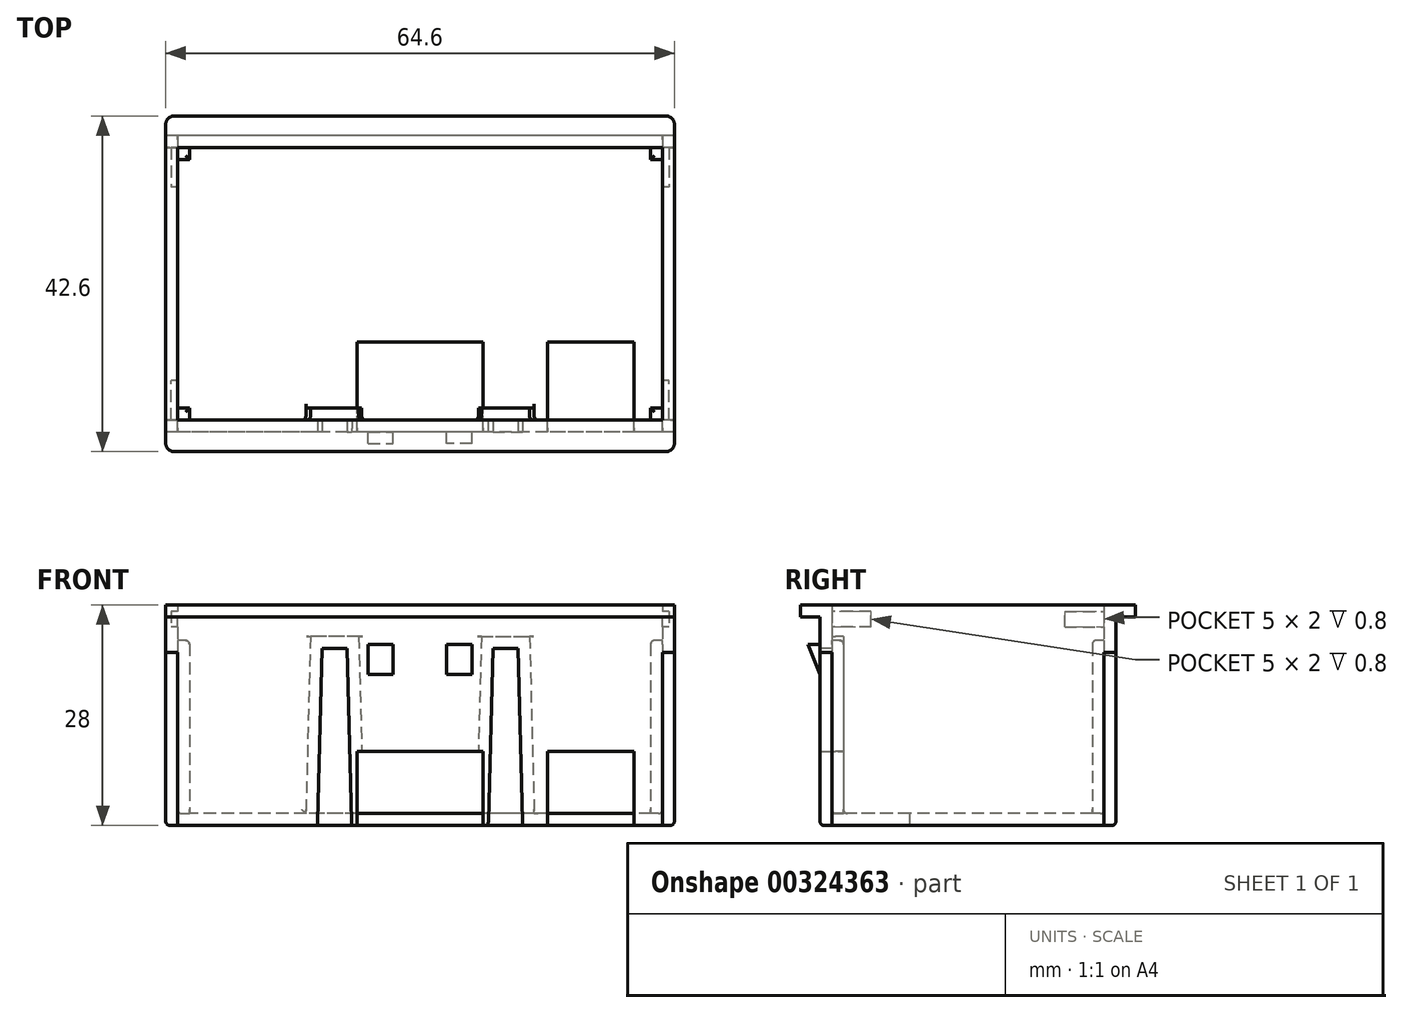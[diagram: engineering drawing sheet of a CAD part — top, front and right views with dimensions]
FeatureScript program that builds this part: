
annotation { "Feature Type Name" : "Feature", "Feature Type Description" : "" }
export const myFeature = defineFeature(function(context is Context, id is Id, definition is map)
    precondition{}
    {
        {
            var Q0;
            Q0=qCreatedBy(makeId("Top.planeOp"),FACE);
            var sketch = newSketch(context, id + "F0", { "sketchPlane" : qUnion([Q0])});
            skLineSegment(sketch, "E0.bottom", {"start": v(32.3, 18.8) * mm, "end": v(-32.3, 18.8) * mm});
            skLineSegment(sketch, "E0.top", {"start": v(32.3, -18.8) * mm, "end": v(-32.3, -18.8) * mm});
            skLineSegment(sketch, "E0.left", {"start": v(32.3, 18.8) * mm, "end": v(32.3, -18.8) * mm});
            skLineSegment(sketch, "E0.right", {"start": v(-32.3, 18.8) * mm, "end": v(-32.3, -18.8) * mm});
            skPoint(sketch, "E0.middle", {"position": v(0, 0) * mm});
            skSolve(sketch);
        }
        {
            var Q0;
            Q0=makeQuery(id+"F0.imprint","IMPRINT",FACE,{"disambiguationData":[TD([[makeQuery(id+"F0.imprint","IMPRINT",EDGE,{"derivedFrom":sQuery(id+"F0.wireOp",EDGE,"E0.bottom")}),1.0]])]});
            extrude(context, id + "F1", {"entities" : qUnion([Q0]), "depth" : 28 * mm});
        }
        {
            var Q0;
            Q0=makeQuery(id+"F1.opExtrude","SWEPT_FACE",FACE,{"disambiguationData":[OSD([sQuery(id+"F0.wireOp",EDGE,"E0.top")])]});
            var sketch = newSketch(context, id + "F2", { "sketchPlane" : qUnion([Q0])});
            skLineSegment(sketch, "E1", {"start": v(0, 0) * mm, "end": v(0, 51.62) * mm, "construction": true});
            skLineSegment(sketch, "E2.0", {"start": v(-8.66, 0) * mm, "end": v(-13.04, 0) * mm});
            skLineSegment(sketch, "E3", {"start": v(-9.25, 22.5) * mm, "end": v(-12.45, 22.5) * mm});
            skLineSegment(sketch, "E4", {"start": v(-12.45, 22.5) * mm, "end": v(-13.04, 0) * mm});
            skPoint(sketch, "E5.orphan", {"position": v(32.3, 0) * mm});
            skPoint(sketch, "E6.orphan", {"position": v(-32.3, 0) * mm});
            skLineSegment(sketch, "E7", {"start": v(-9.25, 22.5) * mm, "end": v(-8.66, 0) * mm});
            skLineSegment(sketch, "E8.MirrorCS", {"start": v(9.25, 22.5) * mm, "end": v(12.45, 22.5) * mm});
            skLineSegment(sketch, "E9.MirrorCS", {"start": v(9.25, 22.5) * mm, "end": v(8.66, 0) * mm});
            skLineSegment(sketch, "E10.MirrorCS", {"start": v(12.45, 22.5) * mm, "end": v(13.04, 0) * mm});
            skLineSegment(sketch, "E11.MirrorCS", {"start": v(8.66, 0) * mm, "end": v(13.04, 0) * mm});
            skSolve(sketch);
        }
        {
            var Q0;
            Q0 = qSketchRegion(id + "F2", true);
            extrude(context, id + "F3", {"entities" : qUnion([Q0]), "operationType" : NewBodyOperationType.REMOVE, "oppositeDirection" : true, "depth" : 1.5 * mm});
        }
        {
            var Q0;
            Q0=makeQuery(id+"F1.opExtrude","CAP_FACE",FACE,{"disambiguationData":[OSD([sQuery(id+"F0.wireOp",EDGE,"E0.bottom"),sQuery(id+"F0.wireOp",EDGE,"E0.top"),sQuery(id+"F0.wireOp",EDGE,"E0.left"),sQuery(id+"F0.wireOp",EDGE,"E0.right")])],"isStart":true});
            var sketch = newSketch(context, id + "F4", { "sketchPlane" : qUnion([Q0])});
            skLineSegment(sketch, "E12.bottom", {"start": v(-32.3, 18.8) * mm, "end": v(-30.8, 18.8) * mm});
            skLineSegment(sketch, "E12.top", {"start": v(-32.3, 17.3) * mm, "end": v(-30.8, 17.3) * mm});
            skLineSegment(sketch, "E12.left", {"start": v(-32.3, 18.8) * mm, "end": v(-32.3, 17.3) * mm});
            skLineSegment(sketch, "E12.right", {"start": v(-30.8, 18.8) * mm, "end": v(-30.8, 17.3) * mm});
            skLineSegment(sketch, "E13.bottom", {"start": v(-32.3, -18.8) * mm, "end": v(-30.8, -18.8) * mm});
            skLineSegment(sketch, "E13.top", {"start": v(-32.3, -17.3) * mm, "end": v(-30.8, -17.3) * mm});
            skLineSegment(sketch, "E13.left", {"start": v(-32.3, -18.8) * mm, "end": v(-32.3, -17.3) * mm});
            skLineSegment(sketch, "E13.right", {"start": v(-30.8, -18.8) * mm, "end": v(-30.8, -17.3) * mm});
            skLineSegment(sketch, "E14.bottom", {"start": v(32.3, 18.8) * mm, "end": v(30.8, 18.8) * mm});
            skLineSegment(sketch, "E14.top", {"start": v(32.3, 17.3) * mm, "end": v(30.8, 17.3) * mm});
            skLineSegment(sketch, "E14.left", {"start": v(32.3, 18.8) * mm, "end": v(32.3, 17.3) * mm});
            skLineSegment(sketch, "E14.right", {"start": v(30.8, 18.8) * mm, "end": v(30.8, 17.3) * mm});
            skLineSegment(sketch, "E15.bottom", {"start": v(32.3, -18.8) * mm, "end": v(30.8, -18.8) * mm});
            skLineSegment(sketch, "E15.top", {"start": v(32.3, -17.3) * mm, "end": v(30.8, -17.3) * mm});
            skLineSegment(sketch, "E15.left", {"start": v(32.3, -18.8) * mm, "end": v(32.3, -17.3) * mm});
            skLineSegment(sketch, "E15.right", {"start": v(30.8, -18.8) * mm, "end": v(30.8, -17.3) * mm});
            skSolve(sketch);
        }
        {
            var Q0;
            Q0=makeQuery(id+"F4.imprint","IMPRINT",FACE,{"disambiguationData":[TD([[makeQuery(id+"F4.imprint","IMPRINT",EDGE,{"derivedFrom":sQuery(id+"F4.wireOp",EDGE,"E12.bottom")}),1.0]])]});
            var Q1;
            Q1=makeQuery(id+"F4.imprint","IMPRINT",FACE,{"disambiguationData":[TD([[makeQuery(id+"F4.imprint","IMPRINT",EDGE,{"derivedFrom":sQuery(id+"F4.wireOp",EDGE,"E14.bottom")}),1.0]])]});
            var Q2;
            Q2=makeQuery(id+"F4.imprint","IMPRINT",FACE,{"disambiguationData":[TD([[makeQuery(id+"F4.imprint","IMPRINT",EDGE,{"derivedFrom":sQuery(id+"F4.wireOp",EDGE,"E15.bottom")}),-1.0]])]});
            var Q3;
            Q3=makeQuery(id+"F4.imprint","IMPRINT",FACE,{"disambiguationData":[TD([[makeQuery(id+"F4.imprint","IMPRINT",EDGE,{"derivedFrom":sQuery(id+"F4.wireOp",EDGE,"E13.bottom")}),-1.0]])]});
            extrude(context, id + "F5", {"entities" : qUnion([Q0, Q1, Q2, Q3]), "operationType" : NewBodyOperationType.REMOVE, "oppositeDirection" : true, "depth" : 22 * mm});
        }
        {
            var Q0;
            Q0=makeQuery(id+"F1.opExtrude","CAP_FACE",FACE,{"disambiguationData":[OSD([sQuery(id+"F0.wireOp",EDGE,"E0.bottom"),sQuery(id+"F0.wireOp",EDGE,"E0.top"),sQuery(id+"F0.wireOp",EDGE,"E0.left"),sQuery(id+"F0.wireOp",EDGE,"E0.right")])],"isStart":false});
            shell(context, id + "F6", {"entities" : qUnion([Q0]), "thickness" : 1.5 * mm});
        }
        {
            var Q0;
            Q0=makeQuery(id+"F1.opExtrude","CAP_FACE",FACE,{"disambiguationData":[OSD([sQuery(id+"F0.wireOp",EDGE,"E0.bottom"),sQuery(id+"F0.wireOp",EDGE,"E0.top"),sQuery(id+"F0.wireOp",EDGE,"E0.left"),sQuery(id+"F0.wireOp",EDGE,"E0.right")])],"isStart":false});
            var sketch = newSketch(context, id + "F7", { "sketchPlane" : qUnion([Q0])});
            skLineSegment(sketch, "E16.bottom", {"start": v(-32.3, -18.8) * mm, "end": v(32.3, -18.8) * mm});
            skLineSegment(sketch, "E16.top", {"start": v(-32.3, -21.3) * mm, "end": v(32.3, -21.3) * mm});
            skLineSegment(sketch, "E16.left", {"start": v(-32.3, -18.8) * mm, "end": v(-32.3, -21.3) * mm});
            skLineSegment(sketch, "E16.right", {"start": v(32.3, -18.8) * mm, "end": v(32.3, -21.3) * mm});
            skLineSegment(sketch, "E17", {"start": v(-32.3, 0) * mm, "end": v(38.05, 0) * mm, "construction": true});
            skPoint(sketch, "E17.endSnap0", {"position": v(-30.8, 0) * mm});
            skLineSegment(sketch, "E18.MirrorCS", {"start": v(32.3, 18.8) * mm, "end": v(32.3, 21.3) * mm});
            skLineSegment(sketch, "E19.MirrorCS", {"start": v(-32.3, 18.8) * mm, "end": v(-32.3, 21.3) * mm});
            skLineSegment(sketch, "E20.MirrorCS", {"start": v(-32.3, 18.8) * mm, "end": v(32.3, 18.8) * mm});
            skLineSegment(sketch, "E21.MirrorCS", {"start": v(-32.3, 21.3) * mm, "end": v(32.3, 21.3) * mm});
            skSolve(sketch);
        }
        {
            var Q0;
            Q0 = qSketchRegion(id + "F7", true);
            extrude(context, id + "F8", {"entities" : qUnion([Q0]), "operationType" : NewBodyOperationType.ADD, "oppositeDirection" : true, "depth" : 1.5 * mm});
        }
        {
            var Q0;
            Q0=qCreatedBy(makeId("Right.planeOp"),FACE);
            var sketch = newSketch(context, id + "F9", { "sketchPlane" : qUnion([Q0])});
            skLineSegment(sketch, "E22.bottom", {"start": v(-17.3, 27.2) * mm, "end": v(-12.3, 27.2) * mm});
            skLineSegment(sketch, "E22.top", {"start": v(-17.3, 25.2) * mm, "end": v(-12.3, 25.2) * mm});
            skLineSegment(sketch, "E22.left", {"start": v(-17.3, 27.2) * mm, "end": v(-17.3, 25.2) * mm});
            skLineSegment(sketch, "E22.right", {"start": v(-12.3, 27.2) * mm, "end": v(-12.3, 25.2) * mm});
            skLineSegment(sketch, "E23", {"start": v(0, 0) * mm, "end": v(0, 19.41) * mm, "construction": true});
            skLineSegment(sketch, "E24.MirrorCS", {"start": v(12.3, 27.2) * mm, "end": v(12.3, 25.2) * mm});
            skLineSegment(sketch, "E25.MirrorCS", {"start": v(17.3, 27.2) * mm, "end": v(17.3, 25.2) * mm});
            skLineSegment(sketch, "E26.MirrorCS", {"start": v(17.3, 25.2) * mm, "end": v(12.3, 25.2) * mm});
            skLineSegment(sketch, "E27.MirrorCS", {"start": v(17.3, 27.2) * mm, "end": v(12.3, 27.2) * mm});
            skSolve(sketch);
        }
        {
            var Q0;
            Q0 = qSketchRegion(id + "F9", true);
            extrude(context, id + "F10", {"entities" : qUnion([Q0]), "operationType" : NewBodyOperationType.REMOVE, "endBound" : BoundingType.SYMMETRIC, "depth" : (61.6 + 1.6) * mm});
        }
        {
            var Q0;
            Q0=makeQuery(id+"F1.opExtrude","SWEPT_FACE",FACE,{"disambiguationData":[OSD([sQuery(id+"F0.wireOp",EDGE,"E0.top")])]});
            var sketch = newSketch(context, id + "F11", { "sketchPlane" : qUnion([Q0])});
            skLineSegment(sketch, "E28.bottom", {"start": v(-6.6, 23) * mm, "end": v(-3.4, 23) * mm});
            skLineSegment(sketch, "E28.top", {"start": v(-6.6, 19.2) * mm, "end": v(-3.4, 19.2) * mm});
            skLineSegment(sketch, "E28.left", {"start": v(-6.6, 23) * mm, "end": v(-6.6, 19.2) * mm});
            skLineSegment(sketch, "E28.right", {"start": v(-3.4, 23) * mm, "end": v(-3.4, 19.2) * mm});
            skLineSegment(sketch, "E29", {"start": v(0, 0) * mm, "end": v(0, 35.84) * mm, "construction": true});
            skPoint(sketch, "E29.endSnap0", {"position": v(0, 0) * mm});
            skLineSegment(sketch, "E30.MirrorCS", {"start": v(3.4, 23) * mm, "end": v(3.4, 19.2) * mm});
            skLineSegment(sketch, "E31.MirrorCS", {"start": v(6.6, 23) * mm, "end": v(6.6, 19.2) * mm});
            skLineSegment(sketch, "E32.MirrorCS", {"start": v(6.6, 19.2) * mm, "end": v(3.4, 19.2) * mm});
            skLineSegment(sketch, "E33.MirrorCS", {"start": v(6.6, 23) * mm, "end": v(3.4, 23) * mm});
            skSolve(sketch);
        }
        {
            var Q0;
            Q0 = qSketchRegion(id + "F11", true);
            extrude(context, id + "F12", {"entities" : qUnion([Q0]), "operationType" : NewBodyOperationType.ADD, "depth" : 1.5 * mm});
        }
        {
            var Q0;
            Q0=makeQuery(id+"F12.opExtrude","SWEPT_FACE",FACE,{"disambiguationData":[OSD([sQuery(id+"F11.wireOp",EDGE,"E31.MirrorCS")])]});
            var sketch = newSketch(context, id + "F13", { "sketchPlane" : qUnion([Q0])});
            skLineSegment(sketch, "E34", {"start": v(-20.3, 23) * mm, "end": v(-18.8, 19.2) * mm});
            skLineSegment(sketch, "E35", {"start": v(-18.8, 19.2) * mm, "end": v(-20.3, 19.2) * mm});
            skLineSegment(sketch, "E36", {"start": v(-20.3, 19.2) * mm, "end": v(-20.3, 23) * mm});
            skSolve(sketch);
        }
        {
            var Q0;
            Q0 = qSketchRegion(id + "F13", true);
            extrude(context, id + "F14", {"entities" : qUnion([Q0]), "operationType" : NewBodyOperationType.REMOVE, "endBound" : BoundingType.THROUGH_ALL, "oppositeDirection" : true, "depth" : 25 * mm});
        }
        {
            var Q0;
            Q0=makeQuery(id+"F1.opExtrude","CAP_FACE",FACE,{"disambiguationData":[OSD([sQuery(id+"F0.wireOp",EDGE,"E0.bottom"),sQuery(id+"F0.wireOp",EDGE,"E0.top"),sQuery(id+"F0.wireOp",EDGE,"E0.left"),sQuery(id+"F0.wireOp",EDGE,"E0.right")])],"isStart":true});
            var sketch = newSketch(context, id + "F15", { "sketchPlane" : qUnion([Q0])});
            skLineSegment(sketch, "E37.bottom", {"start": v(-8, 18.8) * mm, "end": v(8, 18.8) * mm});
            skLineSegment(sketch, "E37.top", {"start": v(-8, 7.4) * mm, "end": v(8, 7.4) * mm});
            skLineSegment(sketch, "E37.left", {"start": v(-8, 18.8) * mm, "end": v(-8, 7.4) * mm});
            skLineSegment(sketch, "E37.right", {"start": v(8, 18.8) * mm, "end": v(8, 7.4) * mm});
            skLineSegment(sketch, "E38", {"start": v(0, -18.8) * mm, "end": v(0, 39.88) * mm, "construction": true});
            skLineSegment(sketch, "E39.bottom", {"start": v(16.2, 18.8) * mm, "end": v(27.2, 18.8) * mm});
            skLineSegment(sketch, "E39.top", {"start": v(16.2, 7.4) * mm, "end": v(27.2, 7.4) * mm});
            skLineSegment(sketch, "E39.left", {"start": v(16.2, 18.8) * mm, "end": v(16.2, 7.4) * mm});
            skLineSegment(sketch, "E39.right", {"start": v(27.2, 18.8) * mm, "end": v(27.2, 7.4) * mm});
            skLineSegment(sketch, "E40", {"start": v(21.7, 18.8) * mm, "end": v(21.7, 31.46) * mm, "construction": true});
            skPoint(sketch, "E40.endSnap0", {"position": v(21.7, 7.4) * mm});
            skSolve(sketch);
        }
        {
            var Q0;
            Q0 = qSketchRegion(id + "F15", true);
            extrude(context, id + "F16", {"entities" : qUnion([Q0]), "operationType" : NewBodyOperationType.REMOVE, "oppositeDirection" : true, "depth" : 9.4 * mm});
        }
        {
            var Q0;
            Q0=makeQuery(id+"F8.opExtrude","SWEPT_EDGE",EDGE,{"disambiguationData":[OSD([sQuery(id+"F7.wireOp",EDGE,"E16.top"),sQuery(id+"F7.wireOp",EDGE,"E16.right")])]});
            var Q1;
            Q1=makeQuery(id+"F8.opExtrude","SWEPT_EDGE",EDGE,{"disambiguationData":[OSD([sQuery(id+"F7.wireOp",EDGE,"E18.MirrorCS"),sQuery(id+"F7.wireOp",EDGE,"E21.MirrorCS")])]});
            var Q2;
            Q2=makeQuery(id+"F8.opExtrude","SWEPT_EDGE",EDGE,{"disambiguationData":[OSD([sQuery(id+"F7.wireOp",EDGE,"E16.top"),sQuery(id+"F7.wireOp",EDGE,"E16.left")])]});
            var Q3;
            Q3=makeQuery(id+"F8.opExtrude","SWEPT_EDGE",EDGE,{"disambiguationData":[OSD([sQuery(id+"F7.wireOp",EDGE,"E19.MirrorCS"),sQuery(id+"F7.wireOp",EDGE,"E21.MirrorCS")])]});
            fillet(context, id + "F17", {"entities" : qUnion([Q0, Q1, Q2, Q3]), "radius" : 1 * mm, "tangentPropagation" : true, "allowEdgeOverflow" : false});
        }
        {
            var Q0;
            Q0=makeQuery(id+"F1.opExtrude","CAP_EDGE",EDGE,{"disambiguationData":[OSD([sQuery(id+"F0.wireOp",EDGE,"E0.left")])],"isStart":true});
            var Q1;
            {var subQ0=sQuery(id+"F0.wireOp",EDGE,"E0.left");var subQ1=sQuery(id+"F0.wireOp",EDGE,"E0.top");Q1=makeQuery(id+"F16.boolean.opBoolean","SPLIT",EDGE,{"disambiguationData":[TD([makeQuery(id+"F5.boolean.opBoolean","COPY",FACE,{"derivedFrom":makeQuery(id+"F5.opExtrude","SWEPT_FACE",FACE,{"disambiguationData":[OSD([sQuery(id+"F4.wireOp",EDGE,"E14.right")])]})})])],"derivedFrom":makeQuery(id+"F3.boolean.opBoolean","SPLIT",EDGE,{"disambiguationData":[TD([makeQuery(id+"F1.opExtrude","SWEPT_FACE",FACE,{"disambiguationData":[OSD([subQ0])]})])],"derivedFrom":makeQuery(id+"F1.opExtrude","CAP_EDGE",EDGE,{"disambiguationData":[OSD([subQ1])],"isStart":true})})});}
            var Q2;
            {var subQ0=sQuery(id+"F0.wireOp",EDGE,"E0.left");var subQ1=sQuery(id+"F0.wireOp",EDGE,"E0.top");var subQ3=makeQuery(id+"F3.opExtrude","SWEPT_FACE",FACE,{"disambiguationData":[OSD([sQuery(id+"F2.wireOp",EDGE,"E10.MirrorCS")])]});Q2=makeQuery(id+"F16.boolean.opBoolean","SPLIT",EDGE,{"disambiguationData":[TD([makeQuery(id+"F3.boolean.opBoolean","COPY",FACE,{"derivedFrom":subQ3})])],"derivedFrom":makeQuery(id+"F3.boolean.opBoolean","SPLIT",EDGE,{"disambiguationData":[TD([makeQuery(id+"F1.opExtrude","SWEPT_FACE",FACE,{"disambiguationData":[OSD([subQ0])]})])],"derivedFrom":makeQuery(id+"F1.opExtrude","CAP_EDGE",EDGE,{"disambiguationData":[OSD([subQ1])],"isStart":true})})});}
            var Q3;
            {var subQ0=sQuery(id+"F0.wireOp",EDGE,"E0.top");var subQ3=makeQuery(id+"F3.opExtrude","SWEPT_FACE",FACE,{"disambiguationData":[OSD([sQuery(id+"F2.wireOp",EDGE,"E7")])]});Q3=makeQuery(id+"F16.boolean.opBoolean","SPLIT",EDGE,{"disambiguationData":[TD([makeQuery(id+"F3.boolean.opBoolean","COPY",FACE,{"derivedFrom":subQ3})])],"derivedFrom":makeQuery(id+"F3.boolean.opBoolean","SPLIT",EDGE,{"disambiguationData":[TD([subQ3])],"derivedFrom":makeQuery(id+"F1.opExtrude","CAP_EDGE",EDGE,{"disambiguationData":[OSD([subQ0])],"isStart":true})})});}
            var Q4;
            {var subQ0=sQuery(id+"F0.wireOp",EDGE,"E0.right");var subQ1=sQuery(id+"F0.wireOp",EDGE,"E0.top");Q4=makeQuery(id+"F3.boolean.opBoolean","SPLIT",EDGE,{"disambiguationData":[TD([makeQuery(id+"F1.opExtrude","SWEPT_FACE",FACE,{"disambiguationData":[OSD([subQ0])]})])],"derivedFrom":makeQuery(id+"F1.opExtrude","CAP_EDGE",EDGE,{"disambiguationData":[OSD([subQ1])],"isStart":true})});}
            var Q5;
            Q5=makeQuery(id+"F1.opExtrude","CAP_EDGE",EDGE,{"disambiguationData":[OSD([sQuery(id+"F0.wireOp",EDGE,"E0.right")])],"isStart":true});
            var Q6;
            {var subQ0=sQuery(id+"F0.wireOp",EDGE,"E0.bottom");var subQ1=sQuery(id+"F0.wireOp",EDGE,"E0.right");Q6=makeQuery(id+"F4bC7VjvYii6qsK_1.1.F3.boolean.opBoolean","SPLIT",EDGE,{"disambiguationData":[TD([makeQuery(id+"F1.opExtrude","SWEPT_FACE",FACE,{"disambiguationData":[OSD([subQ1])]})])],"derivedFrom":makeQuery(id+"F1.opExtrude","CAP_EDGE",EDGE,{"disambiguationData":[OSD([subQ0])],"isStart":true})});}
            var Q7;
            {var subQ0=sQuery(id+"F0.wireOp",EDGE,"E0.bottom");Q7=makeQuery(id+"F4bC7VjvYii6qsK_1.1.F3.boolean.opBoolean","SPLIT",EDGE,{"disambiguationData":[TD([makeQuery(id+"F4bC7VjvYii6qsK_1.1.F3.opExtrude","SWEPT_FACE",FACE,{"disambiguationData":[OSD([sQuery(id+"F2.wireOp",EDGE,"E7")])]})])],"derivedFrom":makeQuery(id+"F1.opExtrude","CAP_EDGE",EDGE,{"disambiguationData":[OSD([subQ0])],"isStart":true})});}
            var Q8;
            {var subQ0=sQuery(id+"F0.wireOp",EDGE,"E0.bottom");var subQ1=sQuery(id+"F0.wireOp",EDGE,"E0.left");Q8=makeQuery(id+"F4bC7VjvYii6qsK_1.1.F3.boolean.opBoolean","SPLIT",EDGE,{"disambiguationData":[TD([makeQuery(id+"F1.opExtrude","SWEPT_FACE",FACE,{"disambiguationData":[OSD([subQ1])]})])],"derivedFrom":makeQuery(id+"F1.opExtrude","CAP_EDGE",EDGE,{"disambiguationData":[OSD([subQ0])],"isStart":true})});}
            var Q9;
            {var subQ0=sQuery(id+"F0.wireOp",EDGE,"E0.top");var subQ3=makeQuery(id+"F3.opExtrude","SWEPT_FACE",FACE,{"disambiguationData":[OSD([sQuery(id+"F2.wireOp",EDGE,"E9.MirrorCS")])]});Q9=makeQuery(id+"F16.boolean.opBoolean","SPLIT",EDGE,{"disambiguationData":[TD([makeQuery(id+"F3.boolean.opBoolean","COPY",FACE,{"derivedFrom":subQ3})])],"derivedFrom":makeQuery(id+"F3.boolean.opBoolean","SPLIT",EDGE,{"disambiguationData":[TD([makeQuery(id+"F3.opExtrude","SWEPT_FACE",FACE,{"disambiguationData":[OSD([sQuery(id+"F2.wireOp",EDGE,"E7")])]})])],"derivedFrom":makeQuery(id+"F1.opExtrude","CAP_EDGE",EDGE,{"disambiguationData":[OSD([subQ0])],"isStart":true})})});}
            fillet(context, id + "F18", {"entities" : qUnion([Q0, Q1, Q2, Q3, Q4, Q5, Q6, Q7, Q8, Q9]), "radius" : 0.5 * mm, "tangentPropagation" : true, "allowEdgeOverflow" : false});
        }
        {
            var Q0;
            {var subQ0=sQuery(id+"F0.wireOp",EDGE,"E0.right");var subQ1=sQuery(id+"F0.wireOp",EDGE,"E0.top");Q0=makeQuery(id+"F6.opShell","OFFSET_EDGE",EDGE,{"disambiguationData":[OSD([subQ1]),TDD([makeQuery(id+"F3.boolean.opBoolean","SPLIT",EDGE,{"disambiguationData":[TD([makeQuery(id+"F1.opExtrude","SWEPT_FACE",FACE,{"disambiguationData":[OSD([subQ0])]})])],"derivedFrom":makeQuery(id+"F1.opExtrude","CAP_EDGE",EDGE,{"disambiguationData":[OSD([subQ1])],"isStart":true})})])]});}
            var Q1;
            {var subQ0=sQuery(id+"F0.wireOp",EDGE,"E0.right");Q1=makeQuery(id+"F6.opShell","OFFSET_EDGE",EDGE,{"disambiguationData":[OSD([subQ0]),TDD([makeQuery(id+"F1.opExtrude","CAP_EDGE",EDGE,{"disambiguationData":[OSD([subQ0])],"isStart":true})])]});}
            var Q2;
            {var subQ0=sQuery(id+"F0.wireOp",EDGE,"E0.bottom");var subQ1=sQuery(id+"F0.wireOp",EDGE,"E0.right");Q2=makeQuery(id+"F6.opShell","OFFSET_EDGE",EDGE,{"disambiguationData":[OSD([subQ0]),TDD([makeQuery(id+"F4bC7VjvYii6qsK_1.1.F3.boolean.opBoolean","SPLIT",EDGE,{"disambiguationData":[TD([makeQuery(id+"F1.opExtrude","SWEPT_FACE",FACE,{"disambiguationData":[OSD([subQ1])]})])],"derivedFrom":makeQuery(id+"F1.opExtrude","CAP_EDGE",EDGE,{"disambiguationData":[OSD([subQ0])],"isStart":true})})])]});}
            var Q3;
            {var subQ0=sQuery(id+"F0.wireOp",EDGE,"E0.bottom");Q3=makeQuery(id+"F6.opShell","OFFSET_EDGE",EDGE,{"disambiguationData":[OSD([subQ0]),TDD([makeQuery(id+"F4bC7VjvYii6qsK_1.1.F3.boolean.opBoolean","SPLIT",EDGE,{"disambiguationData":[TD([makeQuery(id+"F4bC7VjvYii6qsK_1.1.F3.opExtrude","SWEPT_FACE",FACE,{"disambiguationData":[OSD([sQuery(id+"F2.wireOp",EDGE,"E7")])]})])],"derivedFrom":makeQuery(id+"F1.opExtrude","CAP_EDGE",EDGE,{"disambiguationData":[OSD([subQ0])],"isStart":true})})])]});}
            var Q4;
            {var subQ0=sQuery(id+"F0.wireOp",EDGE,"E0.bottom");var subQ1=sQuery(id+"F0.wireOp",EDGE,"E0.left");Q4=makeQuery(id+"F6.opShell","OFFSET_EDGE",EDGE,{"disambiguationData":[OSD([subQ0]),TDD([makeQuery(id+"F4bC7VjvYii6qsK_1.1.F3.boolean.opBoolean","SPLIT",EDGE,{"disambiguationData":[TD([makeQuery(id+"F1.opExtrude","SWEPT_FACE",FACE,{"disambiguationData":[OSD([subQ1])]})])],"derivedFrom":makeQuery(id+"F1.opExtrude","CAP_EDGE",EDGE,{"disambiguationData":[OSD([subQ0])],"isStart":true})})])]});}
            var Q5;
            {var subQ0=sQuery(id+"F0.wireOp",EDGE,"E0.left");Q5=makeQuery(id+"F6.opShell","OFFSET_EDGE",EDGE,{"disambiguationData":[OSD([subQ0]),TDD([makeQuery(id+"F1.opExtrude","CAP_EDGE",EDGE,{"disambiguationData":[OSD([subQ0])],"isStart":true})])]});}
            var Q6;
            {var subQ0=sQuery(id+"F4.wireOp",EDGE,"E12.right");Q6=makeQuery(id+"F6.opShell","OFFSET_EDGE",EDGE,{"disambiguationData":[OSD([subQ0]),TDD([makeQuery(id+"F5.boolean.opBoolean","COPY",EDGE,{"derivedFrom":makeQuery(id+"F5.opExtrude","CAP_EDGE",EDGE,{"disambiguationData":[OSD([subQ0])],"isStart":true})})])]});}
            var Q7;
            {var subQ0=sQuery(id+"F4.wireOp",EDGE,"E12.top");Q7=makeQuery(id+"F6.opShell","OFFSET_EDGE",EDGE,{"disambiguationData":[OSD([subQ0]),TDD([makeQuery(id+"F5.boolean.opBoolean","COPY",EDGE,{"derivedFrom":makeQuery(id+"F5.opExtrude","CAP_EDGE",EDGE,{"disambiguationData":[OSD([subQ0])],"isStart":true})})])]});}
            var Q8;
            {var subQ0=sQuery(id+"F4.wireOp",EDGE,"E13.right");Q8=makeQuery(id+"F6.opShell","OFFSET_EDGE",EDGE,{"disambiguationData":[OSD([subQ0]),TDD([makeQuery(id+"F5.boolean.opBoolean","COPY",EDGE,{"derivedFrom":makeQuery(id+"F5.opExtrude","CAP_EDGE",EDGE,{"disambiguationData":[OSD([subQ0])],"isStart":true})})])]});}
            var Q9;
            {var subQ0=sQuery(id+"F4.wireOp",EDGE,"E13.top");Q9=makeQuery(id+"F6.opShell","OFFSET_EDGE",EDGE,{"disambiguationData":[OSD([subQ0]),TDD([makeQuery(id+"F5.boolean.opBoolean","COPY",EDGE,{"derivedFrom":makeQuery(id+"F5.opExtrude","CAP_EDGE",EDGE,{"disambiguationData":[OSD([subQ0])],"isStart":true})})])]});}
            var Q10;
            {var subQ0=sQuery(id+"F2.wireOp",EDGE,"E2.0");Q10=makeQuery(id+"F6.opShell","OFFSET_EDGE",EDGE,{"disambiguationData":[OSD([subQ0]),TDD([makeQuery(id+"F4bC7VjvYii6qsK_1.1.F3.boolean.opBoolean","COPY",EDGE,{"derivedFrom":makeQuery(id+"F4bC7VjvYii6qsK_1.1.F3.opExtrude","CAP_EDGE",EDGE,{"disambiguationData":[OSD([subQ0])],"isStart":false})})])]});}
            var Q11;
            {var subQ0=sQuery(id+"F2.wireOp",EDGE,"E7");var subQ1=sQuery(id+"F2.wireOp",EDGE,"E2.0");var subQ2=sQuery(id+"F0.wireOp",EDGE,"E0.top");Q11=makeQuery(id+"F6.opShell","OFFSET_EDGE",EDGE,{"disambiguationData":[OSD([subQ2,subQ1,subQ0]),TDD([makeQuery(id+"F4bC7VjvYii6qsK_1.1.F3.boolean.opBoolean","COPY",EDGE,{"derivedFrom":makeQuery(id+"F4bC7VjvYii6qsK_1.1.F3.opExtrude","SWEPT_EDGE",EDGE,{"disambiguationData":[OSD([subQ2,subQ1,subQ0])]})})])]});}
            var Q12;
            {var subQ0=sQuery(id+"F2.wireOp",EDGE,"E4");var subQ1=sQuery(id+"F2.wireOp",EDGE,"E2.0");var subQ2=sQuery(id+"F0.wireOp",EDGE,"E0.top");Q12=makeQuery(id+"F6.opShell","OFFSET_EDGE",EDGE,{"disambiguationData":[OSD([subQ2,subQ1,subQ0]),TDD([makeQuery(id+"F4bC7VjvYii6qsK_1.1.F3.boolean.opBoolean","COPY",EDGE,{"derivedFrom":makeQuery(id+"F4bC7VjvYii6qsK_1.1.F3.opExtrude","SWEPT_EDGE",EDGE,{"disambiguationData":[OSD([subQ2,subQ1,subQ0])]})})])]});}
            var Q13;
            {var subQ0=sQuery(id+"F2.wireOp",EDGE,"E11.MirrorCS");Q13=makeQuery(id+"F6.opShell","OFFSET_EDGE",EDGE,{"disambiguationData":[OSD([subQ0]),TDD([makeQuery(id+"F4bC7VjvYii6qsK_1.1.F3.boolean.opBoolean","COPY",EDGE,{"derivedFrom":makeQuery(id+"F4bC7VjvYii6qsK_1.1.F3.opExtrude","CAP_EDGE",EDGE,{"disambiguationData":[OSD([subQ0])],"isStart":false})})])]});}
            var Q14;
            {var subQ0=sQuery(id+"F2.wireOp",EDGE,"E11.MirrorCS");var subQ1=sQuery(id+"F2.wireOp",EDGE,"E9.MirrorCS");var subQ2=sQuery(id+"F0.wireOp",EDGE,"E0.top");Q14=makeQuery(id+"F6.opShell","OFFSET_EDGE",EDGE,{"disambiguationData":[OSD([subQ2,subQ1,subQ0]),TDD([makeQuery(id+"F4bC7VjvYii6qsK_1.1.F3.boolean.opBoolean","COPY",EDGE,{"derivedFrom":makeQuery(id+"F4bC7VjvYii6qsK_1.1.F3.opExtrude","SWEPT_EDGE",EDGE,{"disambiguationData":[OSD([subQ2,subQ1,subQ0])]})})])]});}
            var Q15;
            {var subQ0=sQuery(id+"F2.wireOp",EDGE,"E11.MirrorCS");var subQ1=sQuery(id+"F2.wireOp",EDGE,"E10.MirrorCS");var subQ2=sQuery(id+"F0.wireOp",EDGE,"E0.top");Q15=makeQuery(id+"F6.opShell","OFFSET_EDGE",EDGE,{"disambiguationData":[OSD([subQ2,subQ1,subQ0]),TDD([makeQuery(id+"F4bC7VjvYii6qsK_1.1.F3.boolean.opBoolean","COPY",EDGE,{"derivedFrom":makeQuery(id+"F4bC7VjvYii6qsK_1.1.F3.opExtrude","SWEPT_EDGE",EDGE,{"disambiguationData":[OSD([subQ2,subQ1,subQ0])]})})])]});}
            var Q16;
            {var subQ0=sQuery(id+"F4.wireOp",EDGE,"E15.right");Q16=makeQuery(id+"F6.opShell","OFFSET_EDGE",EDGE,{"disambiguationData":[OSD([subQ0]),TDD([makeQuery(id+"F5.boolean.opBoolean","COPY",EDGE,{"derivedFrom":makeQuery(id+"F5.opExtrude","CAP_EDGE",EDGE,{"disambiguationData":[OSD([subQ0])],"isStart":true})})])]});}
            var Q17;
            {var subQ0=sQuery(id+"F4.wireOp",EDGE,"E15.top");Q17=makeQuery(id+"F6.opShell","OFFSET_EDGE",EDGE,{"disambiguationData":[OSD([subQ0]),TDD([makeQuery(id+"F5.boolean.opBoolean","COPY",EDGE,{"derivedFrom":makeQuery(id+"F5.opExtrude","CAP_EDGE",EDGE,{"disambiguationData":[OSD([subQ0])],"isStart":true})})])]});}
            var Q18;
            {var subQ0=sQuery(id+"F4.wireOp",EDGE,"E14.right");Q18=makeQuery(id+"F6.opShell","OFFSET_EDGE",EDGE,{"disambiguationData":[OSD([subQ0]),TDD([makeQuery(id+"F5.boolean.opBoolean","COPY",EDGE,{"derivedFrom":makeQuery(id+"F5.opExtrude","CAP_EDGE",EDGE,{"disambiguationData":[OSD([subQ0])],"isStart":true})})])]});}
            var Q19;
            {var subQ0=sQuery(id+"F4.wireOp",EDGE,"E14.top");Q19=makeQuery(id+"F6.opShell","OFFSET_EDGE",EDGE,{"disambiguationData":[OSD([subQ0]),TDD([makeQuery(id+"F5.boolean.opBoolean","COPY",EDGE,{"derivedFrom":makeQuery(id+"F5.opExtrude","CAP_EDGE",EDGE,{"disambiguationData":[OSD([subQ0])],"isStart":true})})])]});}
            var Q20;
            {var subQ1=sQuery(id+"F0.wireOp",EDGE,"E0.left");var subQ2=sQuery(id+"F0.wireOp",EDGE,"E0.top");Q20=makeQuery(id+"F16.boolean.opBoolean","SPLIT",EDGE,{"disambiguationData":[TD([makeQuery(id+"F6.opShell","OFFSET_FACE",FACE,{"disambiguationData":[OSD([sQuery(id+"F4.wireOp",EDGE,"E14.right")])]})])],"derivedFrom":makeQuery(id+"F6.opShell","OFFSET_EDGE",EDGE,{"disambiguationData":[OSD([subQ2]),TDD([makeQuery(id+"F3.boolean.opBoolean","SPLIT",EDGE,{"disambiguationData":[TD([makeQuery(id+"F1.opExtrude","SWEPT_FACE",FACE,{"disambiguationData":[OSD([subQ1])]})])],"derivedFrom":makeQuery(id+"F1.opExtrude","CAP_EDGE",EDGE,{"disambiguationData":[OSD([subQ2])],"isStart":true})})])]})});}
            var Q21;
            {var subQ0=sQuery(id+"F2.wireOp",EDGE,"E11.MirrorCS");Q21=makeQuery(id+"F6.opShell","OFFSET_EDGE",EDGE,{"disambiguationData":[OSD([subQ0]),TDD([makeQuery(id+"F3.boolean.opBoolean","COPY",EDGE,{"derivedFrom":makeQuery(id+"F3.opExtrude","CAP_EDGE",EDGE,{"disambiguationData":[OSD([subQ0])],"isStart":false})})])]});}
            var Q22;
            {var subQ0=sQuery(id+"F2.wireOp",EDGE,"E11.MirrorCS");var subQ1=sQuery(id+"F2.wireOp",EDGE,"E10.MirrorCS");var subQ2=sQuery(id+"F0.wireOp",EDGE,"E0.top");Q22=makeQuery(id+"F6.opShell","OFFSET_EDGE",EDGE,{"disambiguationData":[OSD([subQ2,subQ1,subQ0]),TDD([makeQuery(id+"F3.boolean.opBoolean","COPY",EDGE,{"derivedFrom":makeQuery(id+"F3.opExtrude","SWEPT_EDGE",EDGE,{"disambiguationData":[OSD([subQ2,subQ1,subQ0])]})})])]});}
            var Q23;
            {var subQ0=sQuery(id+"F2.wireOp",EDGE,"E2.0");Q23=makeQuery(id+"F6.opShell","OFFSET_EDGE",EDGE,{"disambiguationData":[OSD([subQ0]),TDD([makeQuery(id+"F3.boolean.opBoolean","COPY",EDGE,{"derivedFrom":makeQuery(id+"F3.opExtrude","CAP_EDGE",EDGE,{"disambiguationData":[OSD([subQ0])],"isStart":false})})])]});}
            var Q24;
            {var subQ0=sQuery(id+"F2.wireOp",EDGE,"E4");var subQ1=sQuery(id+"F2.wireOp",EDGE,"E2.0");var subQ2=sQuery(id+"F0.wireOp",EDGE,"E0.top");Q24=makeQuery(id+"F6.opShell","OFFSET_EDGE",EDGE,{"disambiguationData":[OSD([subQ2,subQ1,subQ0]),TDD([makeQuery(id+"F3.boolean.opBoolean","COPY",EDGE,{"derivedFrom":makeQuery(id+"F3.opExtrude","SWEPT_EDGE",EDGE,{"disambiguationData":[OSD([subQ2,subQ1,subQ0])]})})])]});}
            fillet(context, id + "F19", {"entities" : qUnion([Q0, Q1, Q2, Q3, Q4, Q5, Q6, Q7, Q8, Q9, Q10, Q11, Q12, Q13, Q14, Q15, Q16, Q17, Q18, Q19, Q20, Q21, Q22, Q23, Q24]), "radius" : 0.5 * mm, "tangentPropagation" : true, "allowEdgeOverflow" : false});
        }
    });
